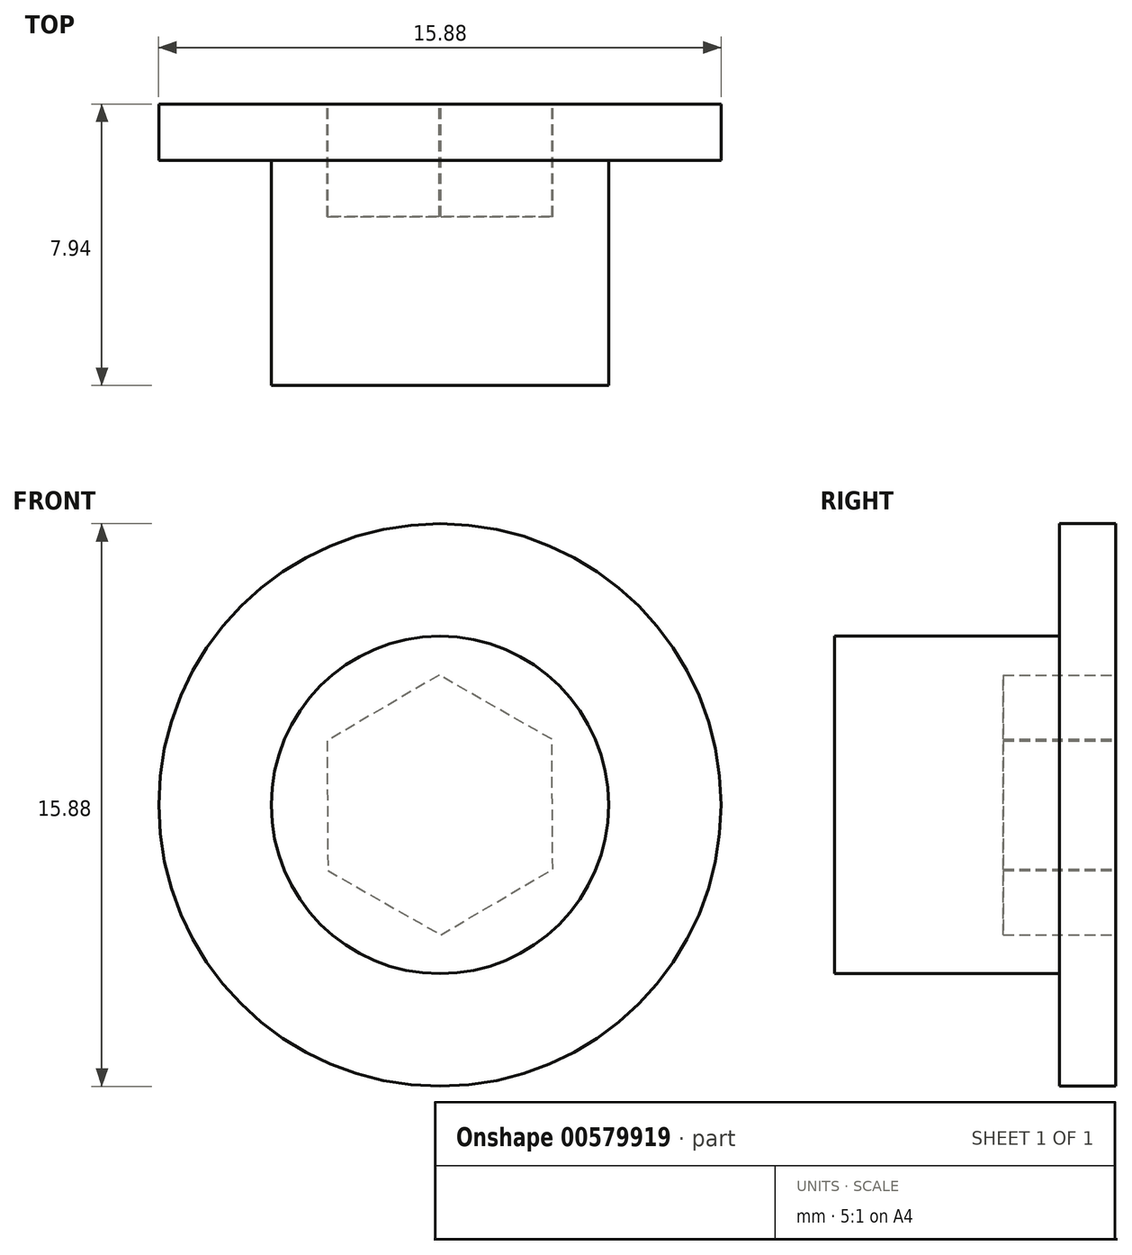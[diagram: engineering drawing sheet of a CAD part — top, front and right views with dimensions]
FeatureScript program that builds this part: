
annotation { "Feature Type Name" : "Feature", "Feature Type Description" : "" }
export const myFeature = defineFeature(function(context is Context, id is Id, definition is map)
    precondition{}
    {
        {
            var Q0;
            Q0=qCreatedBy(makeId("Front.planeOp"),FACE);
            var sketch = newSketch(context, id + "F0", { "sketchPlane" : qUnion([Q0])});
            skCircle(sketch, "E0", {"center": v(0, 0) * mm, "radius": 7.94 * mm});
            skSolve(sketch);
        }
        {
            var Q0;
            Q0 = qSketchRegion(id + "F0", true);
            extrude(context, id + "F1", {"entities" : qUnion([Q0]), "depth" : 1.59 * mm, "offsetDistance" : 25.4 * mm});
        }
        {
            var Q0;
            Q0=makeQuery(id+"F1.opExtrude","CAP_FACE",FACE,{"disambiguationData":[OSD([sQuery(id+"F0.wireOp",EDGE,"E0")])],"isStart":false});
            var sketch = newSketch(context, id + "F2", { "sketchPlane" : qUnion([Q0])});
            skCircle(sketch, "E1", {"center": v(0, 0) * mm, "radius": 4.76 * mm});
            skSolve(sketch);
        }
        {
            var Q0;
            Q0 = qSketchRegion(id + "F2", true);
            extrude(context, id + "F3", {"entities" : qUnion([Q0]), "operationType" : NewBodyOperationType.ADD, "depth" : 6.35 * mm, "offsetDistance" : 25.4 * mm});
        }
        {
            var Q0;
            Q0=makeQuery(id+"F1.opExtrude","CAP_FACE",FACE,{"disambiguationData":[OSD([sQuery(id+"F0.wireOp",EDGE,"E0")])],"isStart":true});
            var sketch = newSketch(context, id + "F4", { "sketchPlane" : qUnion([Q0])});
            skCircle(sketch, "E2.cCircle", {"center": v(0, 0) * mm, "radius": 3.17 * mm, "construction": true});
            skLineSegment(sketch, "E2.0", {"start": v(0.03, 3.67) * mm, "end": v(3.19, 1.81) * mm});
            skLineSegment(sketch, "E2.1", {"start": v(3.19, 1.81) * mm, "end": v(3.16, -1.86) * mm});
            skLineSegment(sketch, "E2.2", {"start": v(3.16, -1.86) * mm, "end": v(-0.03, -3.67) * mm});
            skLineSegment(sketch, "E2.3", {"start": v(-0.03, -3.67) * mm, "end": v(-3.19, -1.81) * mm});
            skLineSegment(sketch, "E2.4", {"start": v(-3.19, -1.81) * mm, "end": v(-3.16, 1.86) * mm});
            skLineSegment(sketch, "E2.5", {"start": v(-3.16, 1.86) * mm, "end": v(0.03, 3.67) * mm});
            skPoint(sketch, "E2.0.midPoint", {"position": v(1.6, 2.74) * mm});
            skSolve(sketch);
        }
        {
            var Q0;
            Q0 = qSketchRegion(id + "F4", true);
            extrude(context, id + "F5", {"entities" : qUnion([Q0]), "operationType" : NewBodyOperationType.REMOVE, "oppositeDirection" : true, "depth" : 3.17 * mm, "offsetDistance" : 25.4 * mm});
        }
    });
